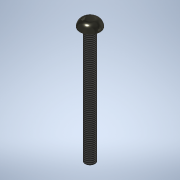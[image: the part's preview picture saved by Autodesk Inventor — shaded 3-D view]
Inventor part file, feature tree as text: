
AUTODESK INVENTOR PART (.ipt)
format: ipt  version: 2020.2 (Build 242310000, 310)  size: 128,512 bytes
history: native  units: mm
features: extrude x4, sketch x4, other x1, fillet x1, thread x1
ambient origin geometry x1: Origin
bodies: Body1 (feature_tree)
feature tree (11):
  other  "ソリッド1"
  extrude  "押し出し1"  Depth=3.0mm
  extrude  "押し出し2"  Depth=6.0mm TaperAngle=0.0deg
  fillet  "フィレット1"  Radius=6.0mm
  thread  "ねじ1"
  extrude  "押し出し3"  Depth=2.0mm TaperAngle=0.0deg
  extrude  "押し出し4"  Depth=2.0mm
  sketch  "スケッチ1"
  sketch  "スケッチ2"
  sketch  "スケッチ3"
  sketch  "スケッチ4"
